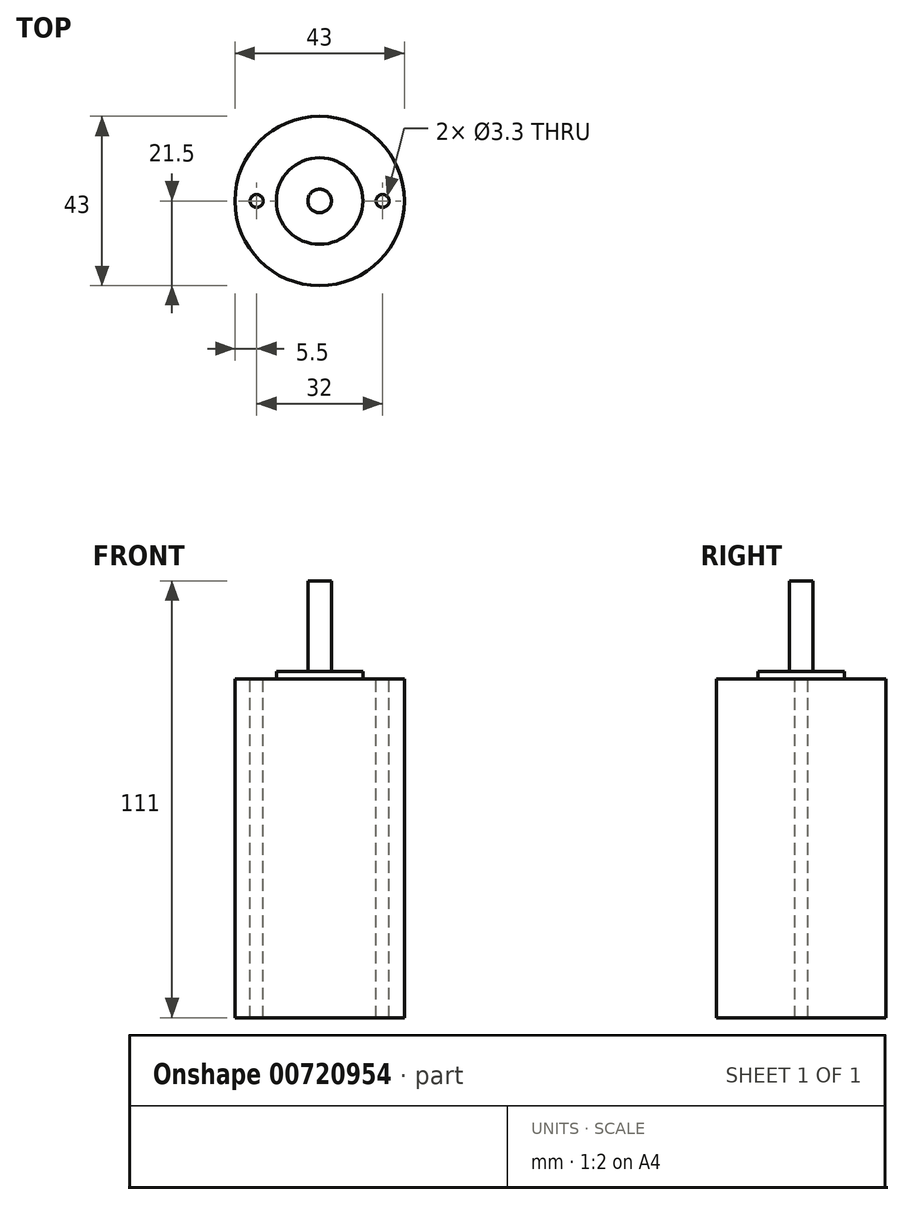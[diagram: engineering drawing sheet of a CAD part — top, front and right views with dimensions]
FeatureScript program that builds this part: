
annotation { "Feature Type Name" : "Feature", "Feature Type Description" : "" }
export const myFeature = defineFeature(function(context is Context, id is Id, definition is map)
    precondition{}
    {
        {
            var Q0;
            Q0=qCreatedBy(makeId("Top.planeOp"),FACE);
            var sketch = newSketch(context, id + "F0", { "sketchPlane" : qUnion([Q0])});
            skCircle(sketch, "E0", {"center": v(0, 0) * mm, "radius": 21.5 * mm});
            skSolve(sketch);
        }
        {
            var Q0;
            Q0 = qSketchRegion(id + "F0", true);
            extrude(context, id + "F1", {"entities" : qUnion([Q0]), "oppositeDirection" : true, "depth" : 86 * mm, "offsetDistance" : 25 * mm});
        }
        {
            var Q0;
            Q0=makeQuery(id+"F1.opExtrude","CAP_FACE",FACE,{"disambiguationData":[OSD([sQuery(id+"F0.wireOp",EDGE,"E0")])],"isStart":true});
            var sketch = newSketch(context, id + "F2", { "sketchPlane" : qUnion([Q0])});
            skCircle(sketch, "E1", {"center": v(0, 0) * mm, "radius": 11 * mm});
            skSolve(sketch);
        }
        {
            var Q0;
            Q0 = qSketchRegion(id + "F2", true);
            extrude(context, id + "F3", {"entities" : qUnion([Q0]), "operationType" : NewBodyOperationType.ADD, "depth" : 2 * mm, "offsetDistance" : 25 * mm});
        }
        {
            var Q0;
            Q0=makeQuery(id+"F3.opExtrude","CAP_FACE",FACE,{"disambiguationData":[OSD([sQuery(id+"F2.wireOp",EDGE,"E1")])],"isStart":false});
            var sketch = newSketch(context, id + "F4", { "sketchPlane" : qUnion([Q0])});
            skCircle(sketch, "E2", {"center": v(0, 0) * mm, "radius": 3 * mm});
            skSolve(sketch);
        }
        {
            var Q0;
            Q0 = qSketchRegion(id + "F4", true);
            extrude(context, id + "F5", {"entities" : qUnion([Q0]), "operationType" : NewBodyOperationType.ADD, "depth" : 23 * mm, "offsetDistance" : 25 * mm});
        }
        {
            var Q0;
            Q0=makeQuery(id+"F1.opExtrude","CAP_FACE",FACE,{"disambiguationData":[OSD([sQuery(id+"F0.wireOp",EDGE,"E0")])],"isStart":true});
            var sketch = newSketch(context, id + "F6", { "sketchPlane" : qUnion([Q0])});
            skCircle(sketch, "E3", {"center": v(0, 0) * mm, "radius": 16 * mm});
            skLineSegment(sketch, "E4", {"start": v(-21.5, 0) * mm, "end": v(21.5, 0) * mm});
            skCircle(sketch, "E5", {"center": v(-16, 0) * mm, "radius": 1.55 * mm});
            skCircle(sketch, "E6", {"center": v(16, 0) * mm, "radius": 1.55 * mm});
            skSolve(sketch);
        }
        {
            var Q0;
            Q0=sQuery(id+"F6.wireOp",VERTEX,"E5.center");
            var Q1;
            Q1=sQuery(id+"F6.wireOp",VERTEX,"E6.center");
            var Q2;
            Q2=makeQuery(id+"F1.opExtrude","SWEPT_BODY",BODY,{"disambiguationData":[OSD([sQuery(id+"F0.wireOp",EDGE,"E0")])]});
            hole(context, id + "F7", {"style" : HoleStyle.SIMPLE, "endStyle" : HoleEndStyle.THROUGH, "standardTappedOrClearance" : lookupTablePath({ "standard" : "ISO", "fit" : "Normal", "size" : "M3", "type" : "Clearance" }), "standardBlindInLast" : lookupTablePath({ "fit" : "Standard", "standard" : "ISO", "size" : "M3", "type" : "Clearance" }), "holeDiameter" : 3.3 * mm, "majorDiameter" : 5 * mm, "isTappedThrough" : true, "tappedDepth" : 12 * mm, "tapClearance" : 3, "locations" : qUnion([Q0, Q1]), "scope" : qUnion([Q2])});
        }
    });
